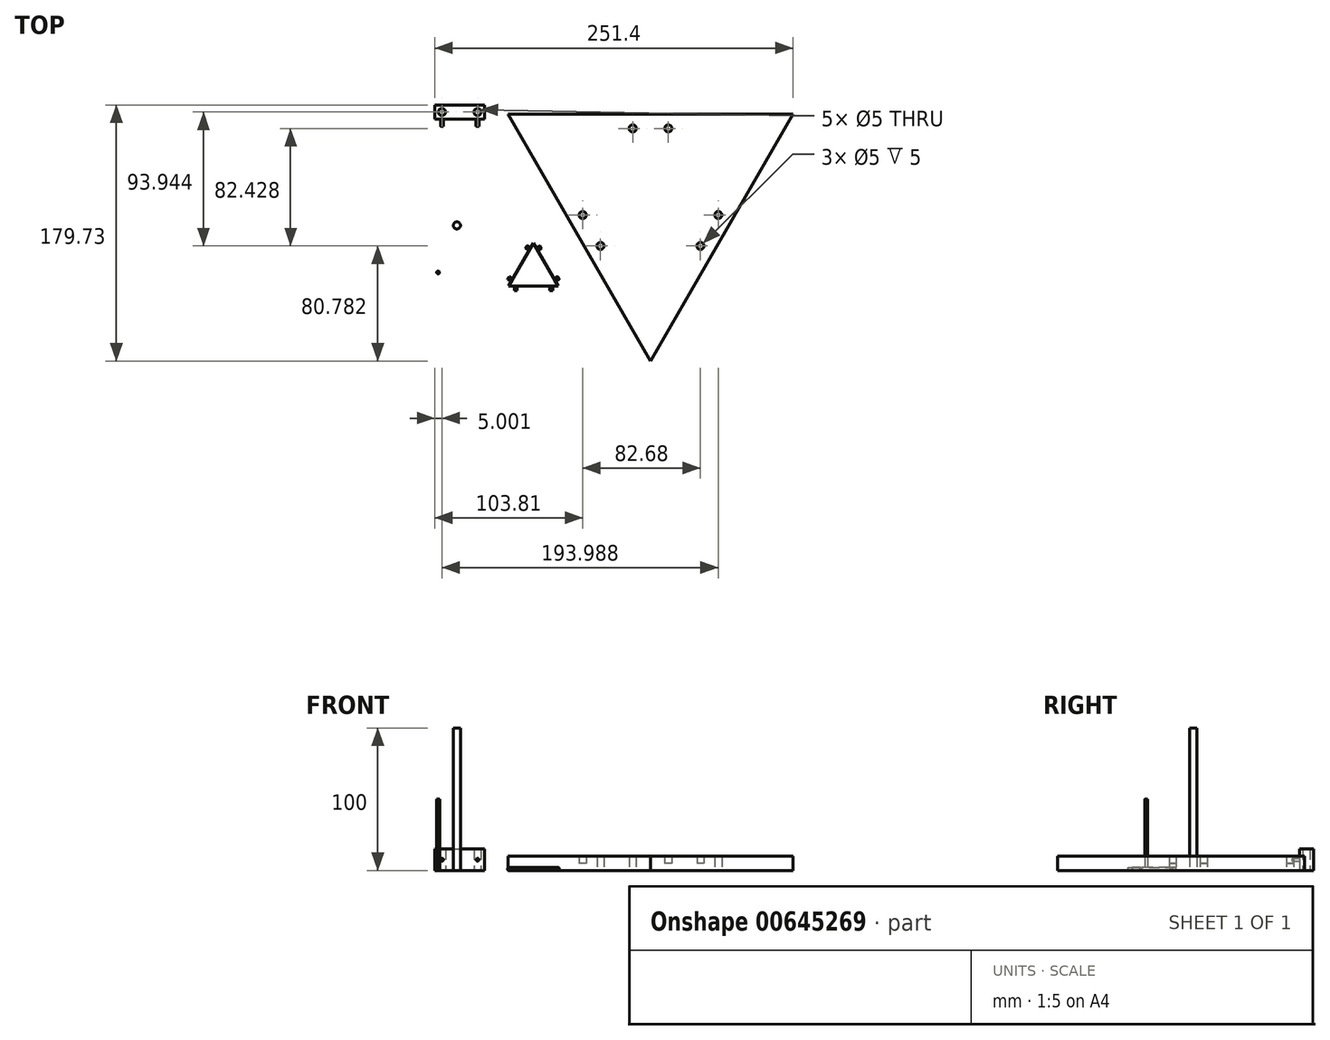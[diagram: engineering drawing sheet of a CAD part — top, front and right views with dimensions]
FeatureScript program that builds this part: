
annotation { "Feature Type Name" : "Feature", "Feature Type Description" : "" }
export const myFeature = defineFeature(function(context is Context, id is Id, definition is map)
    precondition{}
    {
        {
            var Q0;
            Q0=qCreatedBy(makeId("Top.planeOp"),FACE);
            var sketch = newSketch(context, id + "F0", { "sketchPlane" : qUnion([Q0])});
            skCircle(sketch, "E0", {"center": v(-53.72, -28.96) * mm, "radius": 2.5 * mm});
            skLineSegment(sketch, "E1.bottom", {"start": v(-69.22, 55.64) * mm, "end": v(-34.22, 55.64) * mm});
            skLineSegment(sketch, "E1.top", {"start": v(-69.22, 45.64) * mm, "end": v(-34.22, 45.64) * mm});
            skLineSegment(sketch, "E1.left", {"start": v(-69.22, 55.64) * mm, "end": v(-69.22, 45.64) * mm});
            skLineSegment(sketch, "E1.right", {"start": v(-34.22, 55.64) * mm, "end": v(-34.22, 45.64) * mm});
            skCircle(sketch, "E2", {"center": v(-64.22, 50.64) * mm, "radius": 2.5 * mm});
            skPoint(sketch, "E2.centerSnap0", {"position": v(-69.22, 50.64) * mm});
            skLineSegment(sketch, "E3", {"start": v(-51.72, 55.64) * mm, "end": v(-51.72, 33.66) * mm, "construction": true});
            skCircle(sketch, "E4.MirrorC", {"center": v(-39.22, 50.64) * mm, "radius": 2.5 * mm});
            skCircle(sketch, "E5.cCircle", {"center": v(82.18, -8.62) * mm, "radius": 57.74 * mm, "construction": true});
            skLineSegment(sketch, "E5.0", {"start": v(182.18, 49.12) * mm, "end": v(82.18, -124.09) * mm});
            skLineSegment(sketch, "E5.1", {"start": v(82.18, -124.09) * mm, "end": v(-17.82, 49.12) * mm});
            skLineSegment(sketch, "E5.2", {"start": v(-17.82, 49.12) * mm, "end": v(182.18, 49.12) * mm});
            skPoint(sketch, "E5.0.midPoint", {"position": v(132.18, -37.48) * mm});
            skLineSegment(sketch, "E6", {"start": v(82.18, -8.62) * mm, "end": v(82.18, 49.12) * mm, "construction": true});
            skLineSegment(sketch, "E7", {"start": v(82.18, -8.62) * mm, "end": v(132.18, -37.48) * mm, "construction": true});
            skLineSegment(sketch, "E8", {"start": v(82.18, -8.62) * mm, "end": v(32.18, -37.48) * mm, "construction": true});
            skLineSegment(sketch, "E9", {"start": v(30.7, -14.92) * mm, "end": v(52.22, -52.19) * mm, "construction": true});
            skCircle(sketch, "E10", {"center": v(34.59, -21.66) * mm, "radius": 2.5 * mm});
            skCircle(sketch, "E11.MirrorC", {"center": v(47.09, -43.3) * mm, "radius": 2.5 * mm});
            skCircle(sketch, "E12.1.0", {"center": v(117.27, -43.3) * mm, "radius": 2.5 * mm});
            skCircle(sketch, "E12.1.1", {"center": v(129.77, -21.66) * mm, "radius": 2.5 * mm});
            skCircle(sketch, "E12.2.0", {"center": v(94.68, 39.12) * mm, "radius": 2.5 * mm});
            skCircle(sketch, "E12.2.1", {"center": v(69.68, 39.12) * mm, "radius": 2.5 * mm});
            skSolve(sketch);
        }
        {
            var Q0;
            Q0=makeQuery(id+"F0.imprint","IMPRINT",FACE,{"disambiguationData":[TD([[makeQuery(id+"F0.imprint","IMPRINT",EDGE,{"derivedFrom":sQuery(id+"F0.wireOp",EDGE,"E0")}),1.0]])]});
            extrude(context, id + "F1", {"entities" : qUnion([Q0]), "depth" : 100 * mm, "offsetDistance" : 25 * mm});
        }
        {
            var Q0;
            Q0=makeQuery(id+"F0.imprint","IMPRINT",FACE,{"disambiguationData":[TD([[makeQuery(id+"F0.imprint","IMPRINT",EDGE,{"derivedFrom":sQuery(id+"F0.wireOp",EDGE,"E1.bottom")}),-1.0]])]});
            extrude(context, id + "F2", {"entities" : qUnion([Q0]), "depth" : 15 * mm, "offsetDistance" : 25 * mm});
        }
        {
            var Q0;
            Q0=makeQuery(id+"F2.opExtrude","SWEPT_FACE",FACE,{"disambiguationData":[OSD([sQuery(id+"F0.wireOp",EDGE,"E1.top")])]});
            var sketch = newSketch(context, id + "F3", { "sketchPlane" : qUnion([Q0])});
            skCircle(sketch, "E13", {"center": v(-64.22, 7.5) * mm, "radius": 1 * mm});
            skPoint(sketch, "E13.centerSnap0", {"position": v(-69.22, 7.5) * mm});
            skCircle(sketch, "E14", {"center": v(-39.22, 7.5) * mm, "radius": 1 * mm});
            skPoint(sketch, "E14.centerSnap0", {"position": v(-34.22, 7.5) * mm});
            skSolve(sketch);
        }
        {
            var Q0;
            Q0=makeQuery(id+"F3.imprint","IMPRINT",FACE,{"disambiguationData":[TD([[makeQuery(id+"F3.imprint","IMPRINT",EDGE,{"derivedFrom":sQuery(id+"F3.wireOp",EDGE,"E13")}),1.0]])]});
            var Q1;
            Q1=makeQuery(id+"F3.imprint","IMPRINT",FACE,{"disambiguationData":[TD([[makeQuery(id+"F3.imprint","IMPRINT",EDGE,{"derivedFrom":sQuery(id+"F3.wireOp",EDGE,"E14")}),1.0]])]});
            extrude(context, id + "F4", {"entities" : qUnion([Q0, Q1]), "operationType" : NewBodyOperationType.ADD, "depth" : 5 * mm, "offsetDistance" : 25 * mm});
        }
        {
            var Q0;
            Q0=makeQuery(id+"F0.imprint","IMPRINT",FACE,{"disambiguationData":[TD([[makeQuery(id+"F0.imprint","IMPRINT",EDGE,{"derivedFrom":sQuery(id+"F0.wireOp",EDGE,"E5.0")}),-1.0]])]});
            extrude(context, id + "F5", {"entities" : qUnion([Q0]), "depth" : 10 * mm, "offsetDistance" : 25 * mm});
        }
        {
            var Q0;
            Q0=makeQuery(id+"F0.imprint","IMPRINT",FACE,{"disambiguationData":[TD([[makeQuery(id+"F0.imprint","IMPRINT",EDGE,{"derivedFrom":sQuery(id+"F0.wireOp",EDGE,"E12.2.0")}),1.0]])]});
            var Q1;
            Q1=makeQuery(id+"F0.imprint","IMPRINT",FACE,{"disambiguationData":[TD([[makeQuery(id+"F0.imprint","IMPRINT",EDGE,{"derivedFrom":sQuery(id+"F0.wireOp",EDGE,"E12.2.1")}),-1.0]])]});
            var Q2;
            Q2=makeQuery(id+"F0.imprint","IMPRINT",FACE,{"disambiguationData":[TD([[makeQuery(id+"F0.imprint","IMPRINT",EDGE,{"derivedFrom":sQuery(id+"F0.wireOp",EDGE,"E12.1.1")}),-1.0]])]});
            var Q3;
            Q3=makeQuery(id+"F0.imprint","IMPRINT",FACE,{"disambiguationData":[TD([[makeQuery(id+"F0.imprint","IMPRINT",EDGE,{"derivedFrom":sQuery(id+"F0.wireOp",EDGE,"E12.1.0")}),1.0]])]});
            var Q4;
            Q4=makeQuery(id+"F0.imprint","IMPRINT",FACE,{"disambiguationData":[TD([[makeQuery(id+"F0.imprint","IMPRINT",EDGE,{"derivedFrom":sQuery(id+"F0.wireOp",EDGE,"E11.MirrorC")}),-1.0]])]});
            var Q5;
            Q5=makeQuery(id+"F0.imprint","IMPRINT",FACE,{"disambiguationData":[TD([[makeQuery(id+"F0.imprint","IMPRINT",EDGE,{"derivedFrom":sQuery(id+"F0.wireOp",EDGE,"E10")}),1.0]])]});
            extrude(context, id + "F6", {"entities" : qUnion([Q0, Q1, Q2, Q3, Q4, Q5]), "operationType" : NewBodyOperationType.ADD, "depth" : 5 * mm, "offsetDistance" : 25 * mm});
        }
        {
            var Q0;
            Q0=qCreatedBy(makeId("Top.planeOp"),FACE);
            var sketch = newSketch(context, id + "F7", { "sketchPlane" : qUnion([Q0])});
            skCircle(sketch, "E15", {"center": v(-66.9, -61.95) * mm, "radius": 1 * mm});
            skCircle(sketch, "E16.cCircle", {"center": v(0, -61.5) * mm, "radius": 10.1 * mm, "construction": true});
            skLineSegment(sketch, "E16.0", {"start": v(17.5, -71.61) * mm, "end": v(-17.5, -71.61) * mm});
            skLineSegment(sketch, "E16.1", {"start": v(-17.5, -71.61) * mm, "end": v(0, -41.3) * mm});
            skLineSegment(sketch, "E16.2", {"start": v(0, -41.3) * mm, "end": v(17.5, -71.61) * mm});
            skPoint(sketch, "E16.0.midPoint", {"position": v(0, -71.61) * mm});
            skSolve(sketch);
        }
        {
            var Q0;
            Q0=makeQuery(id+"F7.imprint","IMPRINT",FACE,{"disambiguationData":[TD([[makeQuery(id+"F7.imprint","IMPRINT",EDGE,{"derivedFrom":sQuery(id+"F7.wireOp",EDGE,"E15")}),1.0]])]});
            extrude(context, id + "F8", {"entities" : qUnion([Q0]), "depth" : 50 * mm, "offsetDistance" : 25 * mm});
        }
        {
            var Q0;
            Q0=makeQuery(id+"F7.imprint","IMPRINT",FACE,{"disambiguationData":[TD([[makeQuery(id+"F7.imprint","IMPRINT",EDGE,{"derivedFrom":sQuery(id+"F7.wireOp",EDGE,"E16.0")}),-1.0]])]});
            extrude(context, id + "F9", {"entities" : qUnion([Q0]), "depth" : 2 * mm, "offsetDistance" : 25 * mm});
        }
        {
            var Q0;
            Q0=makeQuery(id+"F9.opExtrude","SWEPT_FACE",FACE,{"disambiguationData":[OSD([sQuery(id+"F7.wireOp",EDGE,"E16.0")])]});
            var sketch = newSketch(context, id + "F10", { "sketchPlane" : qUnion([Q0])});
            skCircle(sketch, "E17", {"center": v(-12.5, 1) * mm, "radius": 1 * mm});
            skCircle(sketch, "E18", {"center": v(12.5, 1) * mm, "radius": 1 * mm});
            skSolve(sketch);
        }
        {
            var Q0;
            {var subQ0=sQuery(id+"F10.wireOp",EDGE,"E17");var subQ1=sQuery(id+"F7.wireOp",EDGE,"E16.0");var subQ2=makeQuery(id+"F10.imprint","INTERSECT",VERTEX,{"derivedFrom":[makeQuery(id+"F9.opExtrude","CAP_EDGE",EDGE,{"disambiguationData":[OSD([subQ1])],"isStart":true}),subQ0]});Q0=makeQuery(id+"F10.imprint","IMPRINT",FACE,{"disambiguationData":[TD([[makeQuery(id+"F10.imprint","IMPRINT",EDGE,{"disambiguationData":[TD([[subQ2,1.0]])],"derivedFrom":subQ0}),1.0]])]});}
            var Q1;
            {var subQ0=sQuery(id+"F10.wireOp",EDGE,"E18");var subQ1=sQuery(id+"F7.wireOp",EDGE,"E16.0");var subQ2=makeQuery(id+"F10.imprint","INTERSECT",VERTEX,{"derivedFrom":[makeQuery(id+"F9.opExtrude","CAP_EDGE",EDGE,{"disambiguationData":[OSD([subQ1])],"isStart":true}),subQ0]});Q1=makeQuery(id+"F10.imprint","IMPRINT",FACE,{"disambiguationData":[TD([[makeQuery(id+"F10.imprint","IMPRINT",EDGE,{"disambiguationData":[TD([[subQ2,1.0]])],"derivedFrom":subQ0}),1.0]])]});}
            extrude(context, id + "F11", {"entities" : qUnion([Q0, Q1]), "operationType" : NewBodyOperationType.ADD, "depth" : 3 * mm, "offsetDistance" : 25 * mm});
        }
        {
            var Q0;
            Q0=qCreatedBy(makeId("Right.planeOp"),FACE);
            var sketch = newSketch(context, id + "F12", { "sketchPlane" : qUnion([Q0])});
            skLineSegment(sketch, "E19", {"start": v(-61.5, 0) * mm, "end": v(-61.5, 3.42) * mm});
            skSolve(sketch);
        }
        {
            var Q0;
            Q0=makeQuery(id+"F9.opExtrude","SWEPT_BODY",BODY,{"disambiguationData":[OSD([sQuery(id+"F7.wireOp",EDGE,"E16.0"),sQuery(id+"F7.wireOp",EDGE,"E16.1"),sQuery(id+"F7.wireOp",EDGE,"E16.2")])]});
            var Q1;
            Q1=sQuery(id+"F12.wireOp",EDGE,"E19");
            circularPattern(context, id + "F13", {"operationType" : NewBodyOperationType.ADD, "entities" : qUnion([Q0]), "axis" : qUnion([Q1]), "angle" : 360 * degree, "instanceCount" : 3, "equalSpace" : true});
        }
    });
